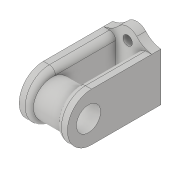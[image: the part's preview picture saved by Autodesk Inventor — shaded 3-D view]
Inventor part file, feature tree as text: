
AUTODESK INVENTOR PART (.ipt)
format: ipt  version: 2018 (Build 220112000, 112)  size: 190,976 bytes
history: native  units: in
note: dims shown in document units (in); Inventor stores cm internally (conversion verified against a paired STEP export)
features: sketch x6, extrude x5, fillet x3, hole x1
ambient origin geometry x8: Origin, YZ Plane, XZ Plane, XY Plane, X Axis, Y Axis, Z Axis, Center Point
bodies: Solid1 (feature_tree)
feature tree (15):
  extrude  "Extrusion1"  Depth=0.1875in TaperAngle=0.0deg
  extrude  "Extrusion2"  Depth=0.25in
  extrude  "Extrusion3"  Depth=1.5in
  fillet  "Fillet1"  Radius=0.75in
  extrude  "Extrusion4"  Depth=0.5in
  extrude  "Extrusion5"  Depth=0.8815in TaperAngle=0.0deg
  fillet  "Fillet2"  Radius=0.5in
  hole  "Hole1"  [1 undecoded]
  fillet  "Fillet3"  Radius=0.8815in
  sketch  "Sketch1"  dims[d1=1.0in d2=0.1875in d3=0.0in]
  sketch  "Sketch2"  dims[d4=0.25in d5=0.25in]
  sketch  "Sketch3"  dims[d6=1.75in d7=0.0in d8=1.5in d9=0.75in]
  sketch  "Sketch4"  dims[d10=1.0in d11=0.5in]
  sketch  "Sketch5"  dims[d12=0.5in d13=0.8815in d14=0.0in d15=0.5in]
  sketch  "Sketch6"  dims[d16=0.501in d17=0.8815in d18=0.0in d19=0.8815in d20=0.0in d21=0.5in d22=0.194in d23=0.75in d24=0.332in d25=0.25in d26=0.5635in d27=1.0in d28=0.8108in d29=0.125in]
note: 1 required parameter value undecoded (feature->parameter linkage not recoverable at this tier; creation-order binding heuristic only, values carry confidence <= 0.55)
